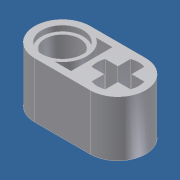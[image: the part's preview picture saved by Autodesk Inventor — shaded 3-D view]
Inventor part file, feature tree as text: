
AUTODESK INVENTOR PART (.ipt)
format: ipt  version: unknown  size: 251,904 bytes
history: native  units: mm
features: extrude x6, sketch x6
ambient origin geometry x8: Origin, YZ Plane, XZ Plane, XY Plane, X Axis, Y Axis, Z Axis, Center Point
bodies: Solid1 (feature_tree)
feature tree (12):
  extrude  "Extrusion1"  Depth=4.0mm
  extrude  "Extrusion10"  TaperAngle=0.0deg  [1 undecoded]
  extrude  "Extrusion11"  TaperAngle=180.0deg  [1 undecoded]
  extrude  "Extrusion12"  Depth=8.0mm TaperAngle=0.0deg
  extrude  "Extrusion13"  Depth=5.0mm
  extrude  "Extrusion14"  Depth=6.0mm
  sketch  "Sketch2"  dims[d0=4.0mm d1=4.0mm]
  sketch  "Sketch11"  dims[d2=8.0mm d3=0.0mm]
  sketch  "Sketch12"  dims[d4=4.0mm d9=180.0deg]
  sketch  "Sketch13"  dims[d10=0.0mm d12=8.0mm d13=0.0mm]
  sketch  "Sketch14"  dims[d98=8.0mm d99=5.0mm]
  sketch  "Sketch15"  dims[d100=10.0mm d101=0.0mm d102=6.0mm d103=0.8mm d104=0.0mm d105=6.0mm d106=0.8mm d107=0.0mm d109=3.0mm d110=3.0mm d111=3.0mm d112=3.0mm d125=0.8mm d126=0.0mm d127=2.0mm d128=2.0mm d129=2.0mm d130=2.0mm d131=1.0mm d132=1.0mm d133=1.0mm d134=1.0mm d135=90.0deg d136=90.0deg d137=90.0deg d138=2.828427mm d139=7.0mm d140=4.25mm d141=10.0mm d142=0.0mm]
note: 2 required parameter values undecoded (feature->parameter linkage not recoverable at this tier; creation-order binding heuristic only, values carry confidence <= 0.55)
